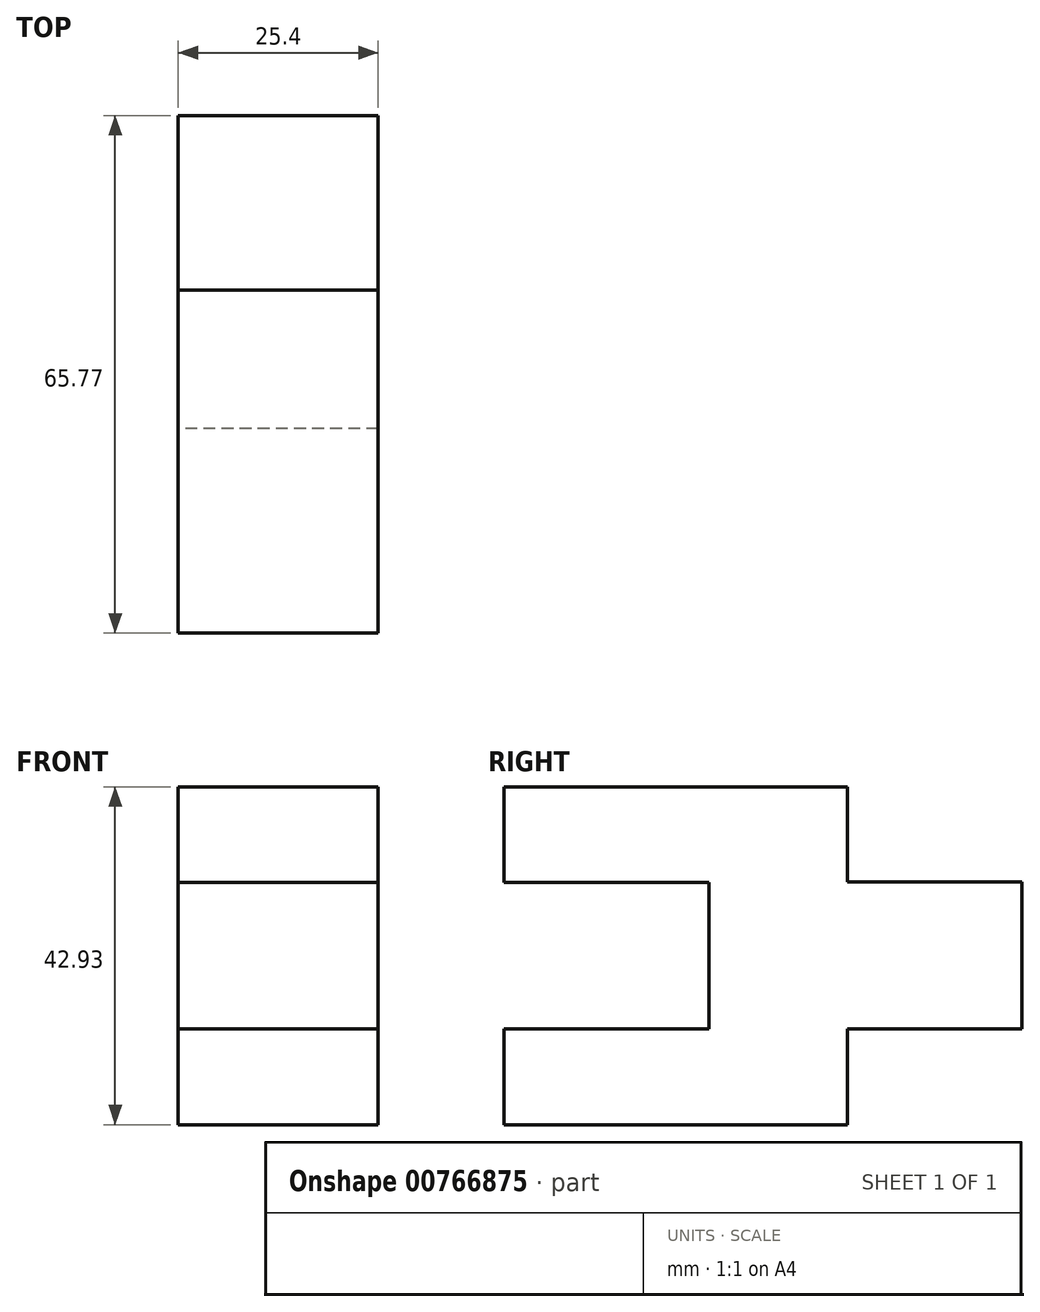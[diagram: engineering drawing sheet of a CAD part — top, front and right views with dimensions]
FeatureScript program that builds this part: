
annotation { "Feature Type Name" : "Feature", "Feature Type Description" : "" }
export const myFeature = defineFeature(function(context is Context, id is Id, definition is map)
    precondition{}
    {
        {
            var Q0;
            Q0=qCreatedBy(makeId("Right.planeOp"),FACE);
            var sketch = newSketch(context, id + "F0", { "sketchPlane" : qUnion([Q0])});
            skLineSegment(sketch, "E0.bottom", {"start": v(0, 0) * mm, "end": v(39.75, 0) * mm});
            skLineSegment(sketch, "E0.top", {"start": v(0, 18.65) * mm, "end": v(39.75, 18.65) * mm});
            skLineSegment(sketch, "E0.left", {"start": v(0, 0) * mm, "end": v(0, 18.65) * mm});
            skLineSegment(sketch, "E0.right", {"start": v(39.75, 0) * mm, "end": v(39.75, 18.65) * mm});
            skSolve(sketch);
        }
        {
            var Q0;
            Q0=makeQuery(id+"F0.imprint","IMPRINT",FACE,{"disambiguationData":[TD([[makeQuery(id+"F0.imprint","IMPRINT",EDGE,{"derivedFrom":sQuery(id+"F0.wireOp",EDGE,"E0.bottom")}),1.0]])]});
            extrude(context, id + "F1", {"entities" : qUnion([Q0]), "depth" : 25.4 * mm, "offsetDistance" : 25.4 * mm});
        }
        {
            var Q0;
            Q0=qCreatedBy(makeId("Right.planeOp"),FACE);
            var sketch = newSketch(context, id + "F2", { "sketchPlane" : qUnion([Q0])});
            skLineSegment(sketch, "E1.bottom", {"start": v(-26.02, 0) * mm, "end": v(0, 0) * mm});
            skLineSegment(sketch, "E1.top", {"start": v(-26.02, -12.18) * mm, "end": v(0, -12.18) * mm});
            skLineSegment(sketch, "E1.left", {"start": v(0, 0) * mm, "end": v(0, -12.18) * mm});
            skLineSegment(sketch, "E1.right", {"start": v(-26.02, 0) * mm, "end": v(-26.02, -12.18) * mm});
            skLineSegment(sketch, "E2.bottom", {"start": v(-26.02, 18.57) * mm, "end": v(0, 18.57) * mm});
            skLineSegment(sketch, "E2.top", {"start": v(-26.02, 30.75) * mm, "end": v(0, 30.75) * mm});
            skLineSegment(sketch, "E2.left", {"start": v(0, 18.57) * mm, "end": v(0, 30.75) * mm});
            skLineSegment(sketch, "E2.right", {"start": v(-26.02, 18.57) * mm, "end": v(-26.02, 30.75) * mm});
            skLineSegment(sketch, "E3.bottom", {"start": v(0, 30.75) * mm, "end": v(17.6, 30.75) * mm});
            skLineSegment(sketch, "E3.top", {"start": v(0, 18.57) * mm, "end": v(17.6, 18.57) * mm});
            skLineSegment(sketch, "E3.left", {"start": v(0, 30.75) * mm, "end": v(0, 18.57) * mm});
            skLineSegment(sketch, "E3.right", {"start": v(17.6, 30.75) * mm, "end": v(17.6, 18.57) * mm});
            skLineSegment(sketch, "E4.bottom", {"start": v(0, 0) * mm, "end": v(17.6, 0) * mm});
            skLineSegment(sketch, "E4.top", {"start": v(0, -12.18) * mm, "end": v(17.6, -12.18) * mm});
            skLineSegment(sketch, "E4.right", {"start": v(17.6, 0) * mm, "end": v(17.6, -12.18) * mm});
            skSolve(sketch);
        }
        {
            var Q0;
            Q0 = qSketchRegion(id + "F2", true);
            extrude(context, id + "F3", {"entities" : qUnion([Q0]), "operationType" : NewBodyOperationType.ADD, "depth" : 25.4 * mm, "offsetDistance" : 25.4 * mm});
        }
    });
